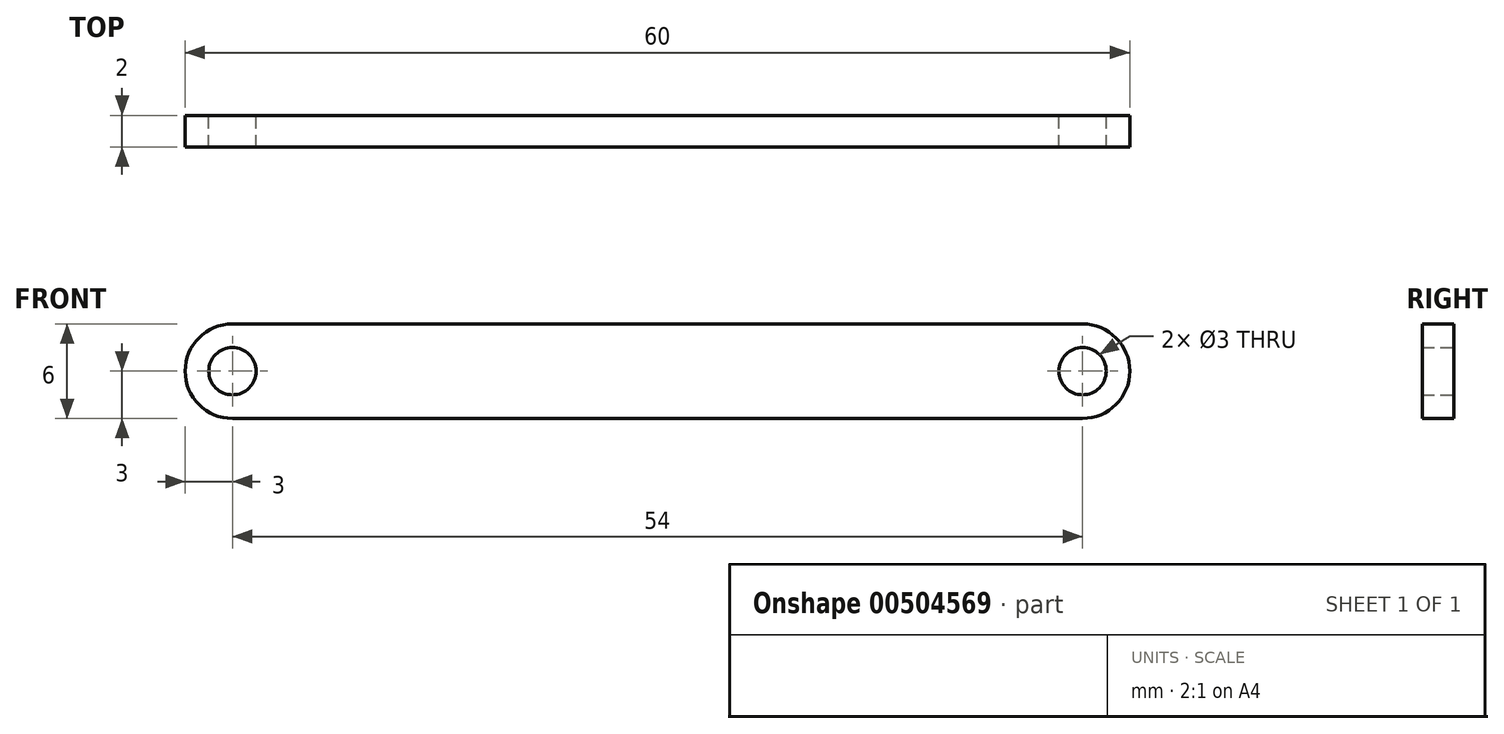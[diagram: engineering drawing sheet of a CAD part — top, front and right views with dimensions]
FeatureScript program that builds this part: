
annotation { "Feature Type Name" : "Feature", "Feature Type Description" : "" }
export const myFeature = defineFeature(function(context is Context, id is Id, definition is map)
    precondition{}
    {
        {
            var Q0;
            Q0=qCreatedBy(makeId("Front.planeOp"),FACE);
            var sketch = newSketch(context, id + "F0", { "sketchPlane" : qUnion([Q0])});
            skLineSegment(sketch, "E0.bottom", {"start": v(27, -3) * mm, "end": v(-27, -3) * mm});
            skLineSegment(sketch, "E0.top", {"start": v(27, 3) * mm, "end": v(-27, 3) * mm});
            skLineSegment(sketch, "E0.left", {"start": v(30, 0) * mm, "end": v(30, 0) * mm});
            skLineSegment(sketch, "E0.right", {"start": v(-30, 0) * mm, "end": v(-30, 0) * mm});
            skPoint(sketch, "E0.middle", {"position": v(0, 0) * mm});
            skPoint(sketch, "E1.visualSharp", {"position": v(30, -3) * mm});
            skArc(sketch, "E1.filletArc", {"start": v(27, -3) * mm, "mid": v(29.12, -2.12) * mm, "end": v(30, 0) * mm});
            skPoint(sketch, "E2.visualSharp", {"position": v(30, 3) * mm});
            skArc(sketch, "E2.filletArc", {"start": v(30, 0) * mm, "mid": v(29.12, 2.12) * mm, "end": v(27, 3) * mm});
            skPoint(sketch, "E3.visualSharp", {"position": v(-30, -3) * mm});
            skArc(sketch, "E3.filletArc", {"start": v(-30, 0) * mm, "mid": v(-29.12, -2.12) * mm, "end": v(-27, -3) * mm});
            skPoint(sketch, "E4.visualSharp", {"position": v(-30, 3) * mm});
            skArc(sketch, "E4.filletArc", {"start": v(-27, 3) * mm, "mid": v(-29.12, 2.12) * mm, "end": v(-30, 0) * mm});
            skCircle(sketch, "E5", {"center": v(-27, 0) * mm, "radius": 1.5 * mm});
            skCircle(sketch, "E6", {"center": v(27, 0) * mm, "radius": 1.5 * mm});
            skSolve(sketch);
        }
        {
            var Q0;
            Q0=makeQuery(id+"F0.imprint","IMPRINT",FACE,{"disambiguationData":[TD([[makeQuery(id+"F0.imprint","IMPRINT",EDGE,{"derivedFrom":sQuery(id+"F0.wireOp",EDGE,"E0.bottom")}),-1.0]])]});
            extrude(context, id + "F1", {"entities" : qUnion([Q0]), "depth" : 2 * mm, "offsetDistance" : 25 * mm});
        }
    });
